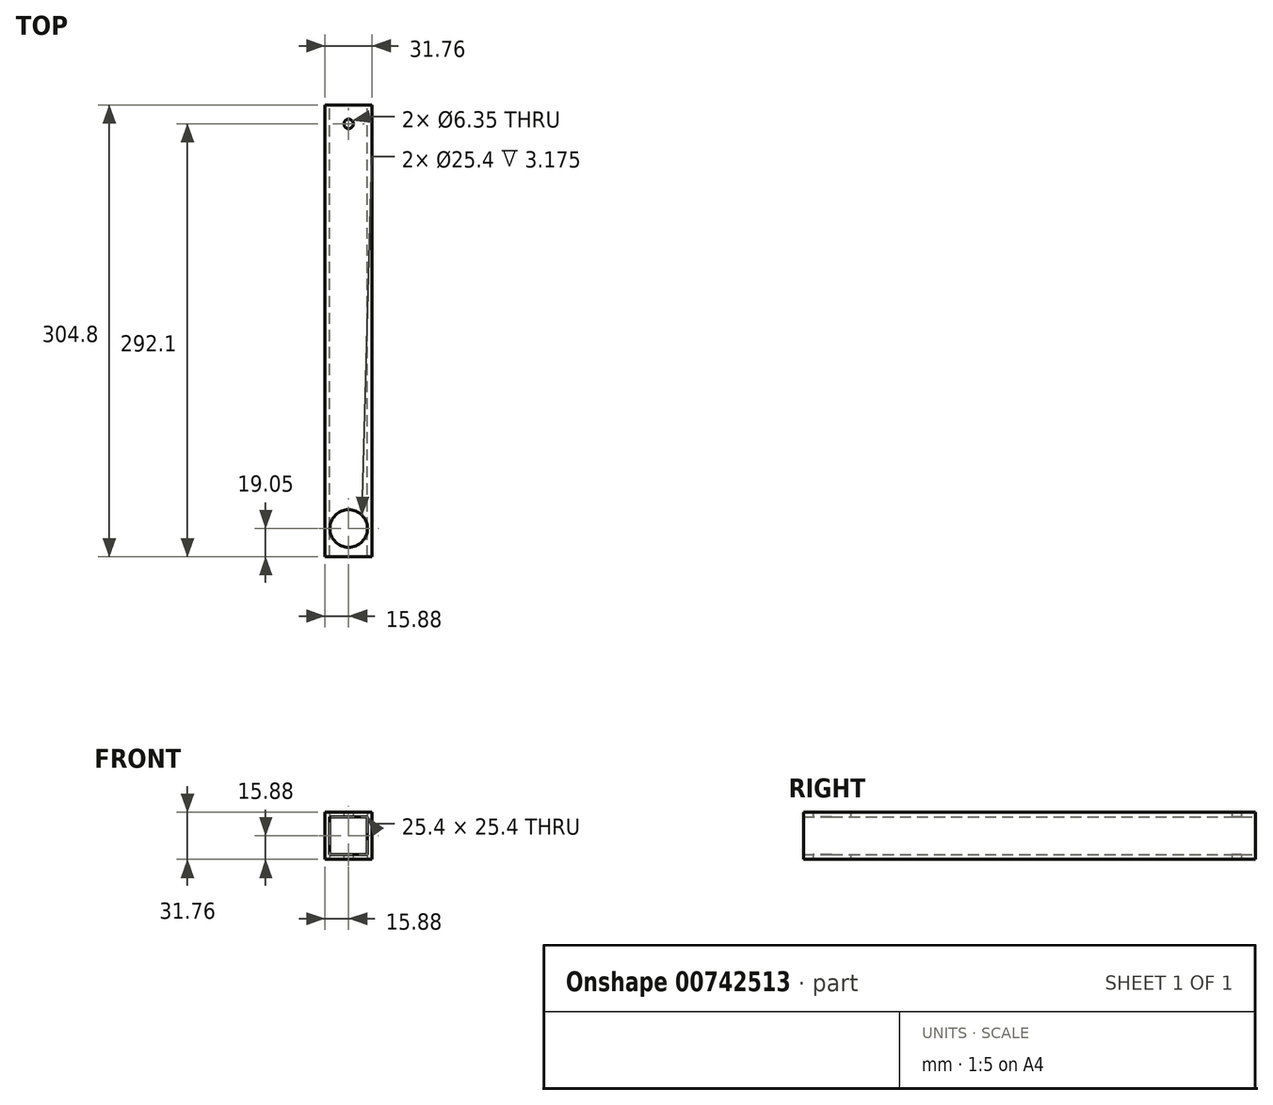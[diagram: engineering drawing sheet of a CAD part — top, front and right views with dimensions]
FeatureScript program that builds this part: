
annotation { "Feature Type Name" : "Feature", "Feature Type Description" : "" }
export const myFeature = defineFeature(function(context is Context, id is Id, definition is map)
    precondition{}
    {
        {
            var Q0;
            Q0=qCreatedBy(makeId("Front.planeOp"),FACE);
            var sketch = newSketch(context, id + "F0", { "sketchPlane" : qUnion([Q0])});
            skLineSegment(sketch, "E0.bottom", {"start": v(12.7, 12.7) * mm, "end": v(-12.7, 12.7) * mm});
            skLineSegment(sketch, "E0.top", {"start": v(12.7, -12.7) * mm, "end": v(-12.7, -12.7) * mm});
            skLineSegment(sketch, "E0.left", {"start": v(12.7, 12.7) * mm, "end": v(12.7, -12.7) * mm});
            skLineSegment(sketch, "E0.right", {"start": v(-12.7, 12.7) * mm, "end": v(-12.7, -12.7) * mm});
            skPoint(sketch, "E0.middle", {"position": v(0, 0) * mm});
            skLineSegment(sketch, "E1.0", {"start": v(15.88, -15.88) * mm, "end": v(-15.88, -15.88) * mm});
            skLineSegment(sketch, "E1.1", {"start": v(15.88, 15.88) * mm, "end": v(15.88, -15.88) * mm});
            skLineSegment(sketch, "E1.2", {"start": v(15.88, 15.88) * mm, "end": v(-15.88, 15.88) * mm});
            skLineSegment(sketch, "E1.3", {"start": v(-15.88, 15.88) * mm, "end": v(-15.88, -15.88) * mm});
            skSolve(sketch);
        }
        {
            var Q0;
            Q0=qSketchRegion(id+"F0",true);
            extrude(context, id + "F1", {"entities" : qUnion([Q0]), "depth" : 304.8 * mm, "offsetDistance" : 25.4 * mm});
        }
        {
            var Q0;
            Q0=makeQuery(id+"F1.opExtrude","SWEPT_FACE",FACE,{"disambiguationData":[OSD([sQuery(id+"F0.wireOp",EDGE,"E1.0")])]});
            var sketch = newSketch(context, id + "F2", { "sketchPlane" : qUnion([Q0])});
            skLineSegment(sketch, "E2", {"start": v(0, 304.8) * mm, "end": v(0, 191.13) * mm, "construction": true});
            skCircle(sketch, "E3", {"center": v(0, 285.75) * mm, "radius": 12.7 * mm});
            skLineSegment(sketch, "E4", {"start": v(0, 0) * mm, "end": v(0, 70.34) * mm});
            skCircle(sketch, "E5", {"center": v(0, 12.7) * mm, "radius": 3.18 * mm});
            skSolve(sketch);
        }
        {
            var Q0;
            Q0=qSketchRegion(id+"F2",true);
            extrude(context, id + "F3", {"entities" : qUnion([Q0]), "operationType" : NewBodyOperationType.REMOVE, "endBound" : BoundingType.THROUGH_ALL, "oppositeDirection" : true, "depth" : 25.4 * mm, "offsetDistance" : 25.4 * mm});
        }
    });
